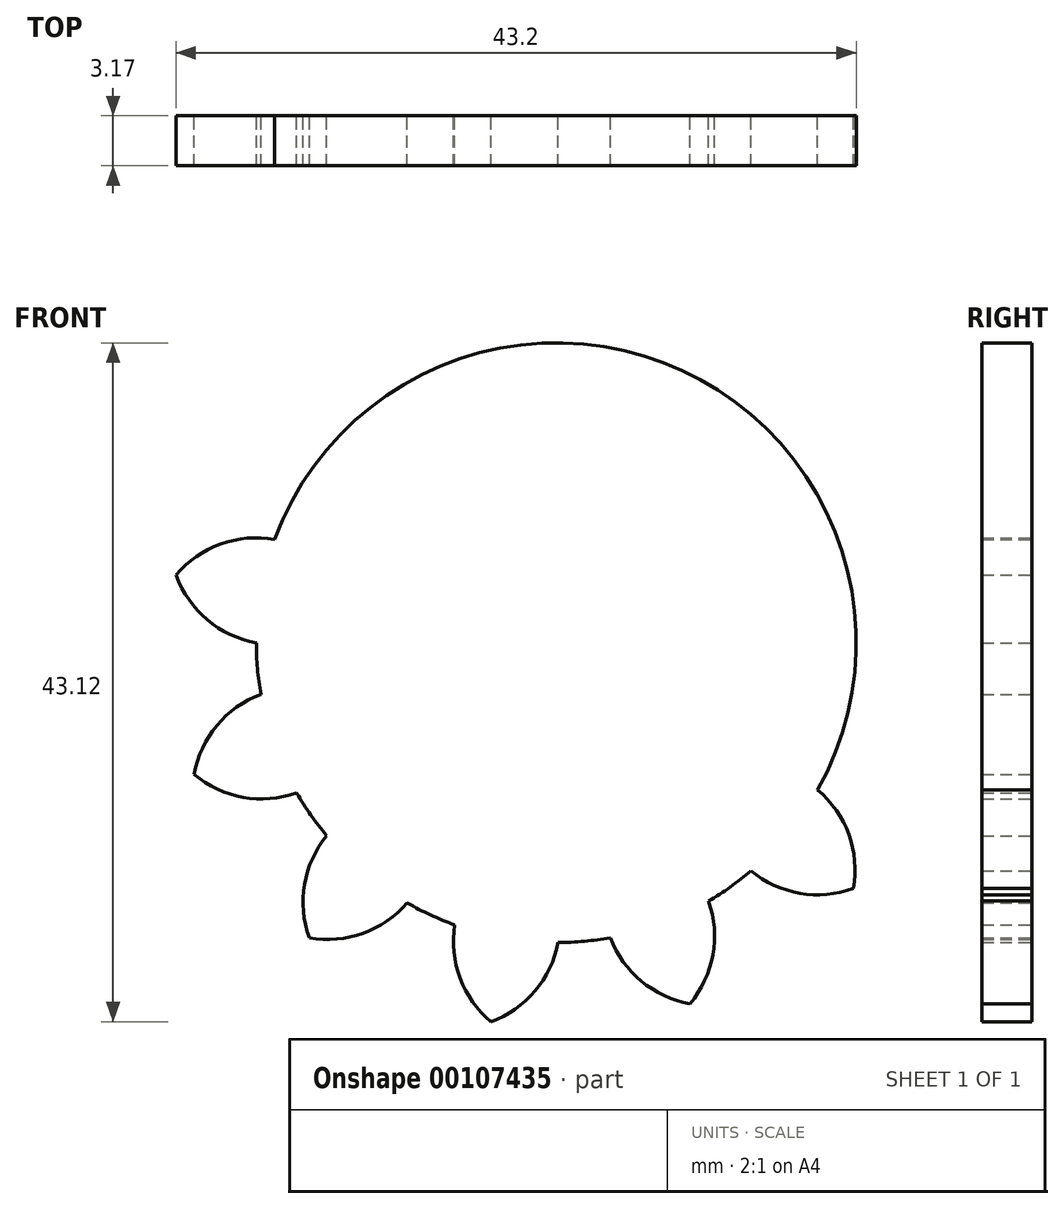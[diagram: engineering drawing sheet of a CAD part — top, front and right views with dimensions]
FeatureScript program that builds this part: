
annotation { "Feature Type Name" : "Feature", "Feature Type Description" : "" }
export const myFeature = defineFeature(function(context is Context, id is Id, definition is map)
    precondition{}
    {
        {
            var Q0;
            Q0=qCreatedBy(makeId("Front.planeOp"),FACE);
            var sketch = newSketch(context, id + "F0", { "sketchPlane" : qUnion([Q0])});
            skCircle(sketch, "E0", {"center": v(0, 0) * mm, "radius": 19.05 * mm});
            skArc(sketch, "E1", {"start": v(-17.89, 6.56) * mm, "mid": v(-21.32, 6.26) * mm, "end": v(-24.15, 4.29) * mm});
            skArc(sketch, "E2", {"start": v(-24.15, 4.29) * mm, "mid": v(-22.17, 1.46) * mm, "end": v(-19.05, 0) * mm});
            skArc(sketch, "E3.1.0", {"start": v(-18.71, -3.26) * mm, "mid": v(-21.54, -5.24) * mm, "end": v(-23, -8.36) * mm});
            skArc(sketch, "E3.1.1", {"start": v(-23, -8.36) * mm, "mid": v(-19.88, -9.82) * mm, "end": v(-16.44, -9.52) * mm});
            skArc(sketch, "E3.2.0", {"start": v(-14.52, -12.18) * mm, "mid": v(-15.98, -15.3) * mm, "end": v(-15.69, -18.74) * mm});
            skArc(sketch, "E3.2.1", {"start": v(-15.69, -18.74) * mm, "mid": v(-12.25, -18.44) * mm, "end": v(-9.42, -16.47) * mm});
            skArc(sketch, "E3.3.0", {"start": v(-6.43, -17.81) * mm, "mid": v(-6.13, -21.25) * mm, "end": v(-4.16, -24.07) * mm});
            skArc(sketch, "E3.3.1", {"start": v(-4.16, -24.07) * mm, "mid": v(-1.33, -22.1) * mm, "end": v(0.13, -18.98) * mm});
            skArc(sketch, "E3.4.0", {"start": v(3.39, -18.64) * mm, "mid": v(5.36, -21.47) * mm, "end": v(8.49, -22.93) * mm});
            skArc(sketch, "E3.4.1", {"start": v(8.49, -22.93) * mm, "mid": v(9.95, -19.8) * mm, "end": v(9.65, -16.37) * mm});
            skArc(sketch, "E3.5.0", {"start": v(12.3, -14.45) * mm, "mid": v(15.43, -15.9) * mm, "end": v(18.87, -15.61) * mm});
            skArc(sketch, "E3.5.1", {"start": v(18.87, -15.61) * mm, "mid": v(18.57, -12.18) * mm, "end": v(16.6, -9.35) * mm});
            skArc(sketch, "E3.6.0", {"start": v(17.94, -6.36) * mm, "mid": v(21.37, -6.06) * mm, "end": v(24.2, -4.09) * mm});
            skArc(sketch, "E3.6.1", {"start": v(24.2, -4.09) * mm, "mid": v(22.23, -1.26) * mm, "end": v(19.1, 0.2) * mm});
            skArc(sketch, "E3.7.0", {"start": v(18.77, 3.46) * mm, "mid": v(21.6, 5.44) * mm, "end": v(23.06, 8.56) * mm});
            skArc(sketch, "E3.7.1", {"start": v(23.06, 8.56) * mm, "mid": v(19.93, 10.02) * mm, "end": v(16.5, 9.73) * mm});
            skArc(sketch, "E3.8.0", {"start": v(14.58, 12.38) * mm, "mid": v(16.04, 15.5) * mm, "end": v(15.74, 18.94) * mm});
            skArc(sketch, "E3.8.1", {"start": v(15.74, 18.94) * mm, "mid": v(12.3, 18.65) * mm, "end": v(9.48, 16.67) * mm});
            skArc(sketch, "E3.9.0", {"start": v(6.48, 18.01) * mm, "mid": v(6.19, 21.45) * mm, "end": v(4.21, 24.28) * mm});
            skArc(sketch, "E3.9.1", {"start": v(4.21, 24.28) * mm, "mid": v(1.39, 22.3) * mm, "end": v(-0.07, 19.18) * mm});
            skArc(sketch, "E3.10.0", {"start": v(-3.34, 18.84) * mm, "mid": v(-5.31, 21.67) * mm, "end": v(-8.43, 23.13) * mm});
            skArc(sketch, "E3.10.1", {"start": v(-8.43, 23.13) * mm, "mid": v(-9.9, 20) * mm, "end": v(-9.6, 16.57) * mm});
            skArc(sketch, "E3.11.0", {"start": v(-12.26, 14.65) * mm, "mid": v(-15.38, 16.11) * mm, "end": v(-18.82, 15.81) * mm});
            skArc(sketch, "E3.11.1", {"start": v(-18.82, 15.81) * mm, "mid": v(-18.52, 12.38) * mm, "end": v(-16.54, 9.55) * mm});
            skPoint(sketch, "E3.center", {"position": v(0.03, 0.1) * mm});
            skSolve(sketch);
        }
        {
            var Q0;
            {var subQ0=sQuery(id+"F0.wireOp",EDGE,"E0");var subQ15=makeQuery(id+"F0.imprint","INTERSECT",VERTEX,{"derivedFrom":[subQ0,sQuery(id+"F0.wireOp",EDGE,"E3.6.1")]});Q0=makeQuery(id+"F0.imprint","IMPRINT",FACE,{"disambiguationData":[TD([[makeQuery(id+"F0.imprint","IMPRINT",EDGE,{"disambiguationData":[TD([[subQ15,-1.0]])],"derivedFrom":subQ0}),1.0]])]});}
            var Q1;
            {var subQ0=sQuery(id+"F0.wireOp",EDGE,"E3.9.0");Q1=makeQuery(id+"F0.imprint","IMPRINT",FACE,{"disambiguationData":[TD([[makeQuery(id+"F0.imprint","IMPRINT",EDGE,{"derivedFrom":subQ0}),1.0]])]});}
            var Q2;
            {var subQ0=sQuery(id+"F0.wireOp",EDGE,"E3.10.0");Q2=makeQuery(id+"F0.imprint","IMPRINT",FACE,{"disambiguationData":[TD([[makeQuery(id+"F0.imprint","IMPRINT",EDGE,{"derivedFrom":subQ0}),1.0]])]});}
            var Q3;
            {var subQ0=sQuery(id+"F0.wireOp",EDGE,"E3.11.0");Q3=makeQuery(id+"F0.imprint","IMPRINT",FACE,{"disambiguationData":[TD([[makeQuery(id+"F0.imprint","IMPRINT",EDGE,{"derivedFrom":subQ0}),1.0]])]});}
            var Q4;
            {var subQ0=sQuery(id+"F0.wireOp",EDGE,"E1");Q4=makeQuery(id+"F0.imprint","IMPRINT",FACE,{"disambiguationData":[TD([[makeQuery(id+"F0.imprint","IMPRINT",EDGE,{"derivedFrom":subQ0}),1.0]])]});}
            var Q5;
            {var subQ0=sQuery(id+"F0.wireOp",EDGE,"E3.1.0");Q5=makeQuery(id+"F0.imprint","IMPRINT",FACE,{"disambiguationData":[TD([[makeQuery(id+"F0.imprint","IMPRINT",EDGE,{"derivedFrom":subQ0}),1.0]])]});}
            var Q6;
            {var subQ0=sQuery(id+"F0.wireOp",EDGE,"E3.2.0");Q6=makeQuery(id+"F0.imprint","IMPRINT",FACE,{"disambiguationData":[TD([[makeQuery(id+"F0.imprint","IMPRINT",EDGE,{"derivedFrom":subQ0}),1.0]])]});}
            var Q7;
            {var subQ0=sQuery(id+"F0.wireOp",EDGE,"E3.3.0");Q7=makeQuery(id+"F0.imprint","IMPRINT",FACE,{"disambiguationData":[TD([[makeQuery(id+"F0.imprint","IMPRINT",EDGE,{"derivedFrom":subQ0}),1.0]])]});}
            var Q8;
            {var subQ0=sQuery(id+"F0.wireOp",EDGE,"E3.4.0");Q8=makeQuery(id+"F0.imprint","IMPRINT",FACE,{"disambiguationData":[TD([[makeQuery(id+"F0.imprint","IMPRINT",EDGE,{"derivedFrom":subQ0}),1.0]])]});}
            var Q9;
            {var subQ0=sQuery(id+"F0.wireOp",EDGE,"E3.5.0");Q9=makeQuery(id+"F0.imprint","IMPRINT",FACE,{"disambiguationData":[TD([[makeQuery(id+"F0.imprint","IMPRINT",EDGE,{"derivedFrom":subQ0}),1.0]])]});}
            var Q10;
            {var subQ0=sQuery(id+"F0.wireOp",EDGE,"E3.6.0");Q10=makeQuery(id+"F0.imprint","IMPRINT",FACE,{"disambiguationData":[TD([[makeQuery(id+"F0.imprint","IMPRINT",EDGE,{"derivedFrom":subQ0}),1.0]])]});}
            var Q11;
            {var subQ0=sQuery(id+"F0.wireOp",EDGE,"E3.7.0");Q11=makeQuery(id+"F0.imprint","IMPRINT",FACE,{"disambiguationData":[TD([[makeQuery(id+"F0.imprint","IMPRINT",EDGE,{"derivedFrom":subQ0}),1.0]])]});}
            var Q12;
            {var subQ0=sQuery(id+"F0.wireOp",EDGE,"E3.8.0");Q12=makeQuery(id+"F0.imprint","IMPRINT",FACE,{"disambiguationData":[TD([[makeQuery(id+"F0.imprint","IMPRINT",EDGE,{"derivedFrom":subQ0}),1.0]])]});}
            extrude(context, id + "F1", {"entities" : qUnion([Q0, Q1, Q2, Q3, Q4, Q5, Q6, Q7, Q8, Q9, Q10, Q11, Q12]), "depth" : 3.17 * mm});
        }
    });
